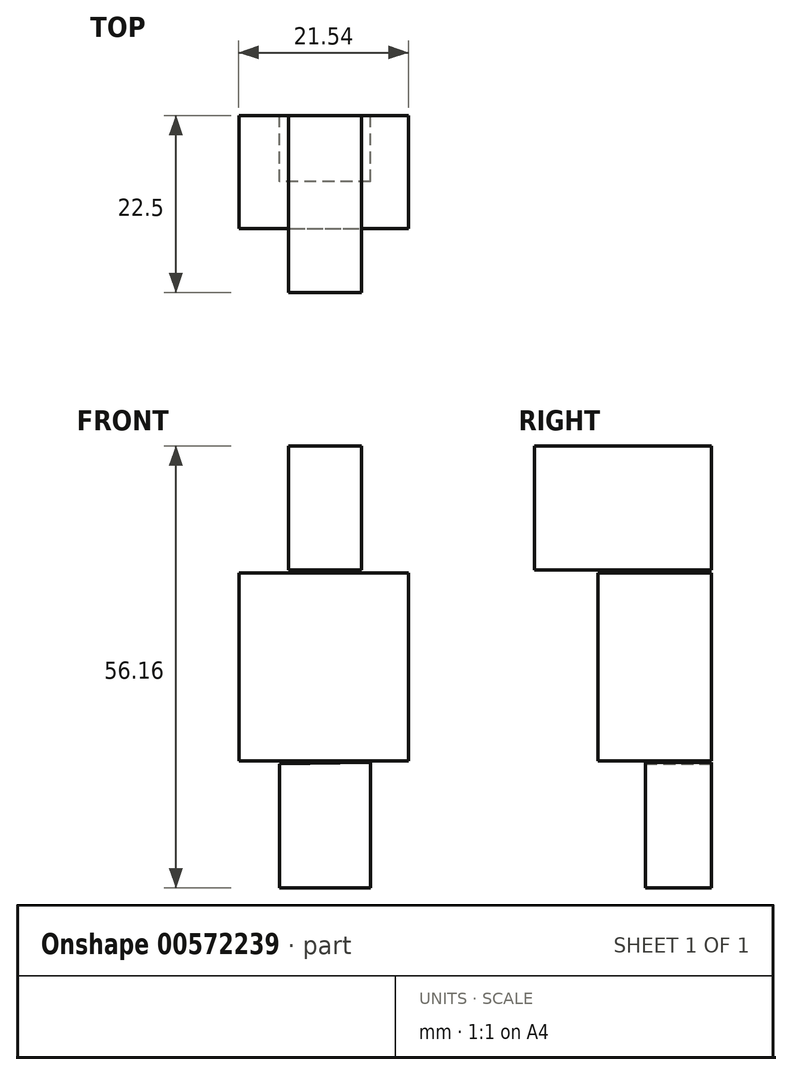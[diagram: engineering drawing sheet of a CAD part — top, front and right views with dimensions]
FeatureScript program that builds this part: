
annotation { "Feature Type Name" : "Feature", "Feature Type Description" : "" }
export const myFeature = defineFeature(function(context is Context, id is Id, definition is map)
    precondition{}
    {
        {
            var Q0;
            Q0=qCreatedBy(makeId("Front.planeOp"),FACE);
            var sketch = newSketch(context, id + "F0", { "sketchPlane" : qUnion([Q0])});
            skLineSegment(sketch, "E0.bottom", {"start": v(-10.77, 9.9) * mm, "end": v(10.77, 9.9) * mm});
            skLineSegment(sketch, "E0.top", {"start": v(-10.77, -13.94) * mm, "end": v(10.77, -13.94) * mm});
            skLineSegment(sketch, "E0.left", {"start": v(-10.77, 9.9) * mm, "end": v(-10.77, -13.94) * mm});
            skLineSegment(sketch, "E0.right", {"start": v(10.77, 9.9) * mm, "end": v(10.77, -13.94) * mm});
            skSolve(sketch);
        }
        {
            var Q0;
            Q0 = qSketchRegion(id + "F0", true);
            extrude(context, id + "F1", {"entities" : qUnion([Q0]), "depth" : 14.4 * mm, "offsetDistance" : 25 * mm});
        }
        {
            var Q0;
            Q0=qCreatedBy(makeId("Front.planeOp"),FACE);
            var sketch = newSketch(context, id + "F2", { "sketchPlane" : qUnion([Q0])});
            skLineSegment(sketch, "E1", {"start": v(-5.58, -14.33) * mm, "end": v(-5.58, -30.1) * mm});
            skLineSegment(sketch, "E2", {"start": v(-5.58, -30.1) * mm, "end": v(5.96, -30.1) * mm});
            skLineSegment(sketch, "E3", {"start": v(5.96, -30.1) * mm, "end": v(5.96, -14.13) * mm});
            skLineSegment(sketch, "E4", {"start": v(5.96, -14.13) * mm, "end": v(-5.58, -14.33) * mm});
            skSolve(sketch);
        }
        {
            var Q0;
            Q0 = qSketchRegion(id + "F2", true);
            extrude(context, id + "F3", {"entities" : qUnion([Q0]), "depth" : 8.4 * mm, "offsetDistance" : 25 * mm});
        }
        {
            var Q0;
            Q0=qCreatedBy(makeId("Front.planeOp"),FACE);
            var sketch = newSketch(context, id + "F4", { "sketchPlane" : qUnion([Q0])});
            skLineSegment(sketch, "E5.bottom", {"start": v(-4.42, 10.29) * mm, "end": v(4.8, 10.29) * mm});
            skLineSegment(sketch, "E5.top", {"start": v(-4.42, 26.06) * mm, "end": v(4.8, 26.06) * mm});
            skLineSegment(sketch, "E5.left", {"start": v(-4.42, 10.29) * mm, "end": v(-4.42, 26.06) * mm});
            skLineSegment(sketch, "E5.right", {"start": v(4.8, 10.29) * mm, "end": v(4.8, 26.06) * mm});
            skSolve(sketch);
        }
        {
            var Q0;
            Q0 = qSketchRegion(id + "F4", true);
            extrude(context, id + "F5", {"entities" : qUnion([Q0]), "depth" : 22.5 * mm, "offsetDistance" : 25 * mm});
        }
    });
